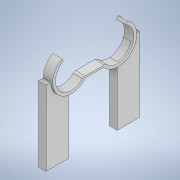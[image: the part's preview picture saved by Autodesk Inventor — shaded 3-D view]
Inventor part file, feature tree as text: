
AUTODESK INVENTOR PART (.ipt)
format: ipt  version: 2022 (Build 260153000, 153)  size: 177,664 bytes
history: native  units: mm
features: extrude x4, sketch x4, plane x1, mirror x1
ambient origin geometry x8: Origin, YZ Plane, XZ Plane, XY Plane, X Axis, Y Axis, Z Axis, Center Point
bodies: Body1 (feature_tree)
feature tree (10):
  extrude  "Extrusion3"  Depth=5.0mm TaperAngle=0.0deg
  plane  "Work Plane3"
  extrude  "Extrusion4"  Depth=40.0mm
  extrude  "Extrusion5"  Depth=9.0mm TaperAngle=0.0deg
  extrude  "Extrusion6"  Depth=4.0mm
  mirror  "Mirror1"
  sketch  "Sketch3"  dims[d18=20.0mm d19=12.5mm d20=2.0mm d21=2.0mm d22=5.0mm d23=0.0mm]
  sketch  "Sketch4"  dims[d25=22.0mm d26=40.0mm]
  sketch  "Sketch5"  dims[d27=3.0mm d28=0.0mm d29=9.0mm d30=0.0mm]
  sketch  "Sketch6"  dims[d31=4.0mm d32=0.0mm d24=0.5mm]
